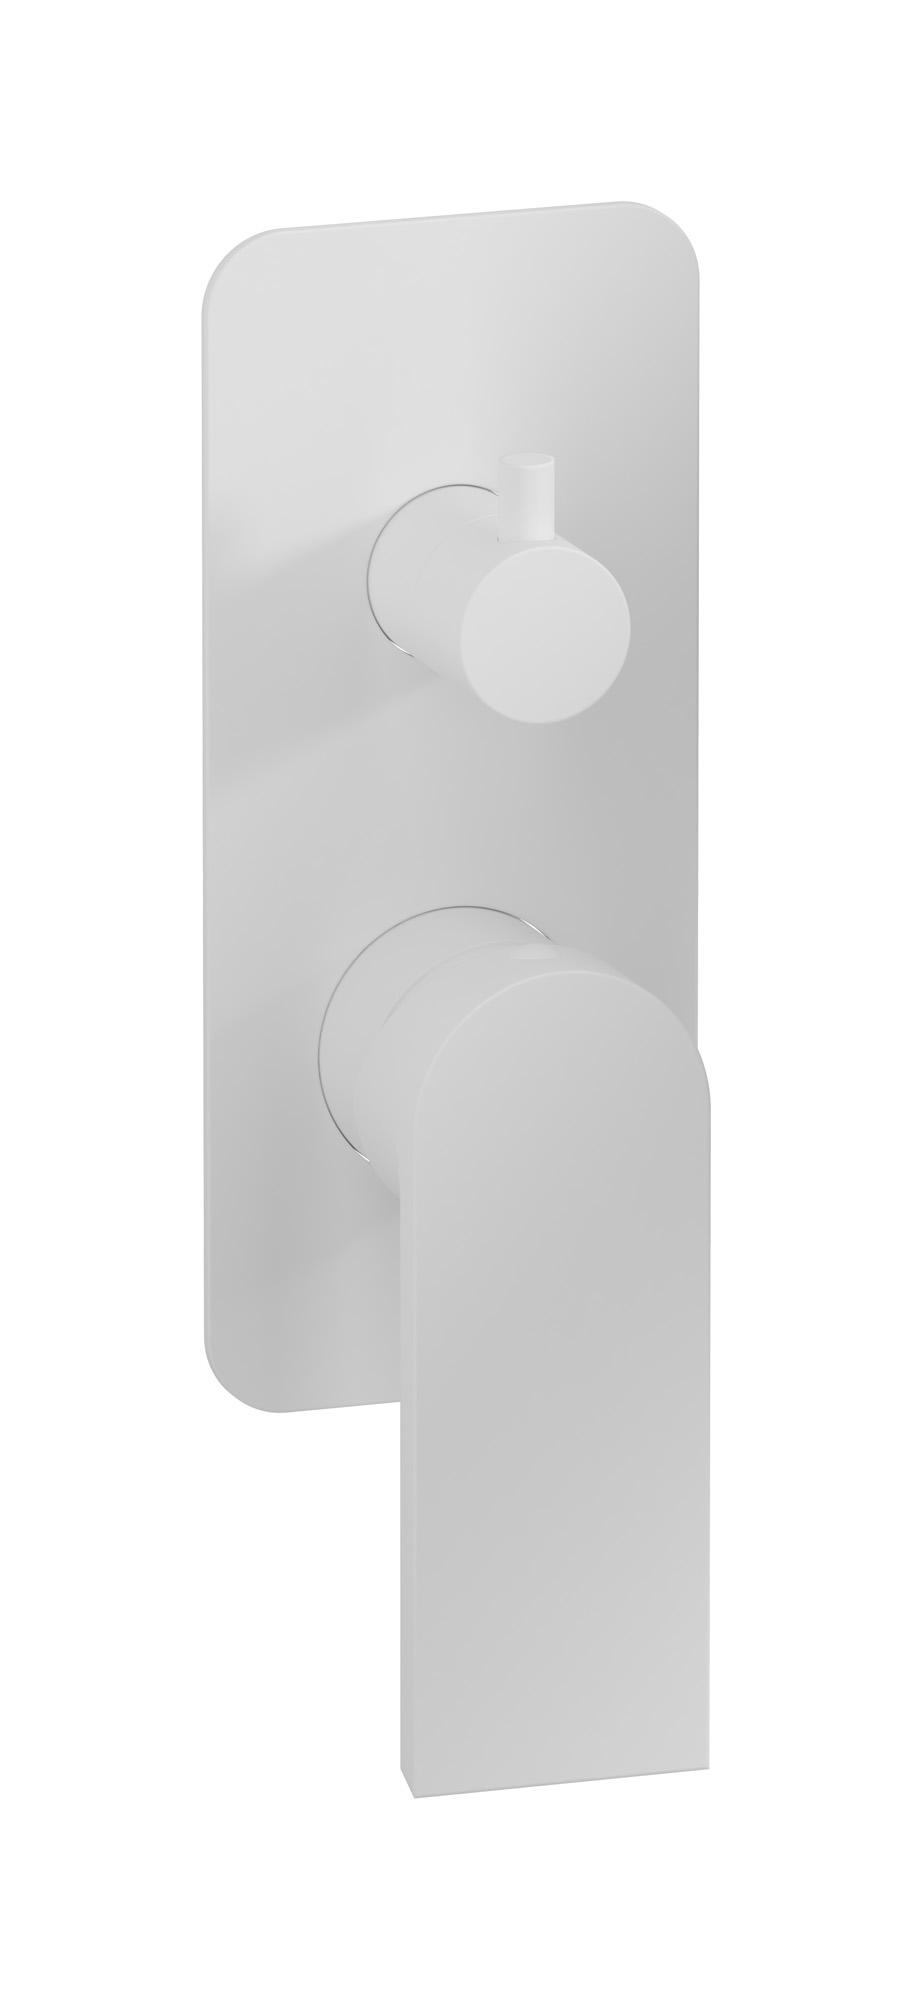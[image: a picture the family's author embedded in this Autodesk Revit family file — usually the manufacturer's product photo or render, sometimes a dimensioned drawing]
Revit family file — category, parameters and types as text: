
# Revit family: K3312
name_source: partatom
category: Apparecchi idraulici
units: mm (PartAtom-declared; Revit-internal decimal feet)

## family parameters
Basato su piano di lavoro = No
Condiviso = No
Mantieni orientamento annotazione = No
Numero OmniClass = 23.45.55.17
Punto di calcolo locali = No
Quota connettore circolare = Usa diametro
Sempre verticale = Sì
Taglio con vuoti quando caricato = No
Tipo di parte = Normale
Titolo OmniClass = Mixing Faucets

## types (8) — shared parameters
Cold water inlet = 10 mm  [stored 0.0328084 ft]
Commenti sul tipo = Wall mixer
Connessione CW = No
Connessione HW = No
Connessione di scarico = No
Connessione di ventilazione = No
Descrizione = Exposed parts for manual wall mixer with three ways diverter
Hot water inlet = 10 mm  [stored 0.0328084 ft]
Produttore = IB Rubinetterie S.p.A.
URL = https://www.weareib.it
zero-valued in all types: Prospetto di default

## per-type parameters (varying)
| type | Finishes surface | Immagine tipo | Modello |
| Chrome | IB_Chrome | K3312CC.jpg | K3312CC |
| Brushed nickel | IB_Brushed nickel | K3312SS.jpg | K3312SS |
| Matt black | IB_matt black | K3312NP.jpg | K3312NP |
| Matt white | IB_matt white | K3312BO.jpg | K3312BO |
| Pale gold | IB_Pale gold | K3312II.jpg | K3312II |
| Brushed pale gold | IB_brushed pale gold | K3312IS.jpg | K3312IS |
| Rose gold | IB_Rose gold | K3312RS.jpg | K3312RS |
| Gold | IB_gold | K3312OO.jpg | K3312OO |

note: [stored X ft] marks values corroborated as IEEE doubles in the binary element streams (Revit-internal decimal feet)
